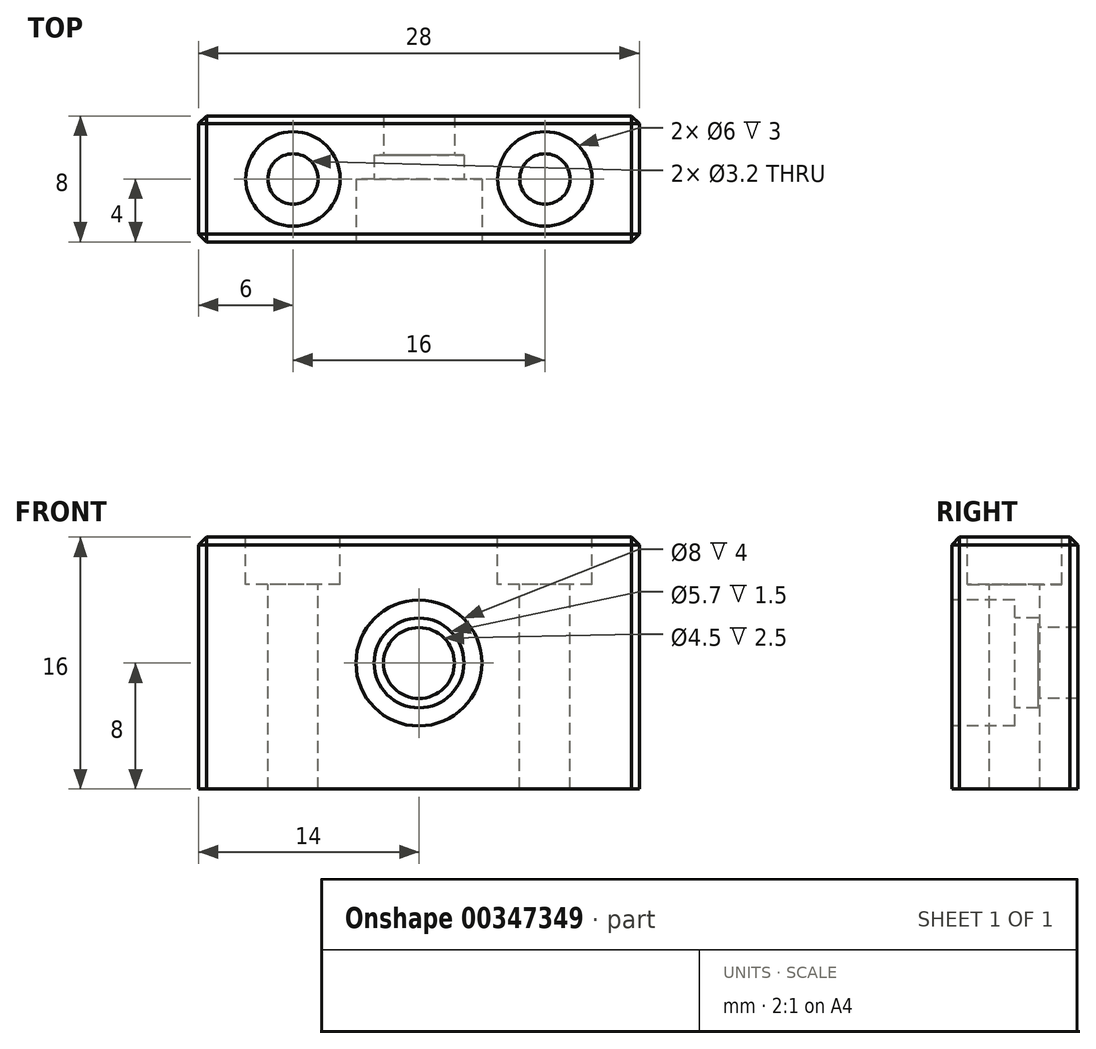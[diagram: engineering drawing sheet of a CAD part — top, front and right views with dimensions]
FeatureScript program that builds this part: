
annotation { "Feature Type Name" : "Feature", "Feature Type Description" : "" }
export const myFeature = defineFeature(function(context is Context, id is Id, definition is map)
    precondition{}
    {
        {
            var Q0;
            Q0=qCreatedBy(makeId("Front.planeOp"),FACE);
            var sketch = newSketch(context, id + "F0", { "sketchPlane" : qUnion([Q0])});
            skLineSegment(sketch, "E0.bottom", {"start": v(0, 0) * mm, "end": v(28, 0) * mm});
            skLineSegment(sketch, "E0.top", {"start": v(0, 16) * mm, "end": v(28, 16) * mm});
            skLineSegment(sketch, "E0.left", {"start": v(0, 0) * mm, "end": v(0, 16) * mm});
            skLineSegment(sketch, "E0.right", {"start": v(28, 0) * mm, "end": v(28, 16) * mm});
            skSolve(sketch);
        }
        {
            var Q0;
            Q0=makeQuery(id+"F0.imprint","IMPRINT",FACE,{"disambiguationData":[TD([[makeQuery(id+"F0.imprint","IMPRINT",EDGE,{"derivedFrom":sQuery(id+"F0.wireOp",EDGE,"E0.bottom")}),1.0]])]});
            extrude(context, id + "F1", {"entities" : qUnion([Q0]), "depth" : 8 * mm});
        }
        {
            var Q0;
            Q0=makeQuery(id+"F1.opExtrude","CAP_FACE",FACE,{"disambiguationData":[OSD([sQuery(id+"F0.wireOp",EDGE,"E0.bottom"),sQuery(id+"F0.wireOp",EDGE,"E0.top"),sQuery(id+"F0.wireOp",EDGE,"E0.left"),sQuery(id+"F0.wireOp",EDGE,"E0.right")])],"isStart":false});
            var sketch = newSketch(context, id + "F2", { "sketchPlane" : qUnion([Q0])});
            skCircle(sketch, "E1", {"center": v(14, 8) * mm, "radius": 4 * mm});
            skSolve(sketch);
        }
        {
            var Q0;
            Q0=makeQuery(id+"F2.imprint","IMPRINT",FACE,{"disambiguationData":[TD([[makeQuery(id+"F2.imprint","IMPRINT",EDGE,{"derivedFrom":sQuery(id+"F2.wireOp",EDGE,"E1")}),1.0]])]});
            extrude(context, id + "F3", {"entities" : qUnion([Q0]), "operationType" : NewBodyOperationType.REMOVE, "oppositeDirection" : true, "depth" : 4 * mm});
        }
        {
            var Q0;
            Q0=makeQuery(id+"F3.boolean.opBoolean","COPY",FACE,{"derivedFrom":makeQuery(id+"F3.opExtrude","CAP_FACE",FACE,{"disambiguationData":[OSD([sQuery(id+"F2.wireOp",EDGE,"E1")])],"isStart":false})});
            var sketch = newSketch(context, id + "F4", { "sketchPlane" : qUnion([Q0])});
            skCircle(sketch, "E2", {"center": v(14, 8) * mm, "radius": 2.85 * mm});
            skSolve(sketch);
        }
        {
            var Q0;
            Q0=makeQuery(id+"F4.imprint","IMPRINT",FACE,{"disambiguationData":[TD([[makeQuery(id+"F4.imprint","IMPRINT",EDGE,{"derivedFrom":sQuery(id+"F4.wireOp",EDGE,"E2")}),1.0]])]});
            var Q1;
            Q1=sQuery(id+"F4.wireOp",EDGE,"E2");
            extrude(context, id + "F5", {"entities" : qUnion([Q0]), "operationType" : NewBodyOperationType.REMOVE, "surfaceEntities" : qUnion([Q1]), "oppositeDirection" : true, "depth" : 1.5 * mm});
        }
        {
            var Q0;
            Q0=makeQuery(id+"F5.boolean.opBoolean","COPY",FACE,{"derivedFrom":makeQuery(id+"F5.opExtrude","CAP_FACE",FACE,{"disambiguationData":[OSD([sQuery(id+"F4.wireOp",EDGE,"E2")])],"isStart":false})});
            var sketch = newSketch(context, id + "F6", { "sketchPlane" : qUnion([Q0])});
            skCircle(sketch, "E3", {"center": v(14, 8) * mm, "radius": 2.25 * mm});
            skSolve(sketch);
        }
        {
            var Q0;
            Q0=makeQuery(id+"F6.imprint","IMPRINT",FACE,{"disambiguationData":[TD([[makeQuery(id+"F6.imprint","IMPRINT",EDGE,{"derivedFrom":sQuery(id+"F6.wireOp",EDGE,"E3")}),1.0]])]});
            var Q1;
            Q1=sQuery(id+"F6.wireOp",EDGE,"E3");
            extrude(context, id + "F7", {"entities" : qUnion([Q0]), "operationType" : NewBodyOperationType.REMOVE, "surfaceEntities" : qUnion([Q1]), "oppositeDirection" : true, "depth" : 25 * mm});
        }
        {
            var Q0;
            Q0=makeQuery(id+"F1.opExtrude","SWEPT_FACE",FACE,{"disambiguationData":[OSD([sQuery(id+"F0.wireOp",EDGE,"E0.top")])]});
            var sketch = newSketch(context, id + "F8", { "sketchPlane" : qUnion([Q0])});
            skCircle(sketch, "E4", {"center": v(6, -4) * mm, "radius": 3 * mm});
            skSolve(sketch);
        }
        {
            var Q0;
            Q0=makeQuery(id+"F8.imprint","IMPRINT",FACE,{"disambiguationData":[TD([[makeQuery(id+"F8.imprint","IMPRINT",EDGE,{"derivedFrom":sQuery(id+"F8.wireOp",EDGE,"E4")}),-1.0]])]});
            var sketch = newSketch(context, id + "F9", { "sketchPlane" : qUnion([Q0])});
            skCircle(sketch, "E5", {"center": v(22, -4) * mm, "radius": 3 * mm});
            skSolve(sketch);
        }
        {
            var Q0;
            Q0=makeQuery(id+"F8.imprint","IMPRINT",FACE,{"disambiguationData":[TD([[makeQuery(id+"F8.imprint","IMPRINT",EDGE,{"derivedFrom":sQuery(id+"F8.wireOp",EDGE,"E4")}),1.0]])]});
            var Q1;
            Q1=sQuery(id+"F8.wireOp",EDGE,"E4");
            extrude(context, id + "F10", {"entities" : qUnion([Q0]), "operationType" : NewBodyOperationType.REMOVE, "surfaceEntities" : qUnion([Q1]), "oppositeDirection" : true, "depth" : 3 * mm});
        }
        {
            var Q0;
            Q0=makeQuery(id+"F9.imprint","IMPRINT",FACE,{"disambiguationData":[TD([[makeQuery(id+"F9.imprint","IMPRINT",EDGE,{"derivedFrom":sQuery(id+"F9.wireOp",EDGE,"E5")}),1.0]])]});
            var Q1;
            Q1=sQuery(id+"F9.wireOp",EDGE,"E5");
            extrude(context, id + "F11", {"entities" : qUnion([Q0]), "operationType" : NewBodyOperationType.REMOVE, "surfaceEntities" : qUnion([Q1]), "oppositeDirection" : true, "depth" : 3 * mm});
        }
        {
            var Q0;
            Q0=makeQuery(id+"F10.boolean.opBoolean","COPY",FACE,{"derivedFrom":makeQuery(id+"F10.opExtrude","CAP_FACE",FACE,{"disambiguationData":[OSD([sQuery(id+"F8.wireOp",EDGE,"E4")])],"isStart":false})});
            var sketch = newSketch(context, id + "F12", { "sketchPlane" : qUnion([Q0])});
            skCircle(sketch, "E6", {"center": v(6, -4) * mm, "radius": 1.6 * mm});
            skSolve(sketch);
        }
        {
            var Q0;
            Q0=makeQuery(id+"F11.boolean.opBoolean","COPY",FACE,{"derivedFrom":makeQuery(id+"F11.opExtrude","CAP_FACE",FACE,{"disambiguationData":[OSD([sQuery(id+"F9.wireOp",EDGE,"E5")])],"isStart":false})});
            var sketch = newSketch(context, id + "F13", { "sketchPlane" : qUnion([Q0])});
            skCircle(sketch, "E7", {"center": v(22, -4) * mm, "radius": 1.6 * mm});
            skSolve(sketch);
        }
        {
            var Q0;
            Q0=makeQuery(id+"F12.imprint","IMPRINT",FACE,{"disambiguationData":[TD([[makeQuery(id+"F12.imprint","IMPRINT",EDGE,{"derivedFrom":sQuery(id+"F12.wireOp",EDGE,"E6")}),1.0]])]});
            var Q1;
            Q1=sQuery(id+"F12.wireOp",EDGE,"E6");
            extrude(context, id + "F14", {"entities" : qUnion([Q0]), "operationType" : NewBodyOperationType.REMOVE, "surfaceEntities" : qUnion([Q1]), "oppositeDirection" : true, "depth" : 25 * mm});
        }
        {
            var Q0;
            Q0=makeQuery(id+"F13.imprint","IMPRINT",FACE,{"disambiguationData":[TD([[makeQuery(id+"F13.imprint","IMPRINT",EDGE,{"derivedFrom":sQuery(id+"F13.wireOp",EDGE,"E7")}),1.0]])]});
            var Q1;
            Q1=sQuery(id+"F13.wireOp",EDGE,"E7");
            extrude(context, id + "F15", {"entities" : qUnion([Q0]), "operationType" : NewBodyOperationType.REMOVE, "surfaceEntities" : qUnion([Q1]), "oppositeDirection" : true, "depth" : 25 * mm});
        }
        {
            var Q0;
            Q0=makeQuery(id+"F1.opExtrude","CAP_EDGE",EDGE,{"disambiguationData":[OSD([sQuery(id+"F0.wireOp",EDGE,"E0.right")])],"isStart":false});
            var Q1;
            Q1=makeQuery(id+"F1.opExtrude","SWEPT_EDGE",EDGE,{"disambiguationData":[OSD([sQuery(id+"F0.wireOp",EDGE,"E0.top"),sQuery(id+"F0.wireOp",EDGE,"E0.right")])]});
            var Q2;
            Q2=makeQuery(id+"F1.opExtrude","CAP_EDGE",EDGE,{"disambiguationData":[OSD([sQuery(id+"F0.wireOp",EDGE,"E0.right")])],"isStart":true});
            var Q3;
            Q3=makeQuery(id+"F1.opExtrude","CAP_EDGE",EDGE,{"disambiguationData":[OSD([sQuery(id+"F0.wireOp",EDGE,"E0.top")])],"isStart":false});
            var Q4;
            Q4=makeQuery(id+"F1.opExtrude","CAP_EDGE",EDGE,{"disambiguationData":[OSD([sQuery(id+"F0.wireOp",EDGE,"E0.top")])],"isStart":true});
            var Q5;
            Q5=makeQuery(id+"F1.opExtrude","SWEPT_EDGE",EDGE,{"disambiguationData":[OSD([sQuery(id+"F0.wireOp",EDGE,"E0.top"),sQuery(id+"F0.wireOp",EDGE,"E0.left")])]});
            var Q6;
            Q6=makeQuery(id+"F1.opExtrude","CAP_EDGE",EDGE,{"disambiguationData":[OSD([sQuery(id+"F0.wireOp",EDGE,"E0.left")])],"isStart":false});
            var Q7;
            Q7=makeQuery(id+"F1.opExtrude","CAP_EDGE",EDGE,{"disambiguationData":[OSD([sQuery(id+"F0.wireOp",EDGE,"E0.left")])],"isStart":true});
            chamfer(context, id + "F16", {"entities" : qUnion([Q0, Q1, Q2, Q3, Q4, Q5, Q6, Q7]), "width" : 0.5 * mm, "tangentPropagation" : true});
        }
    });
